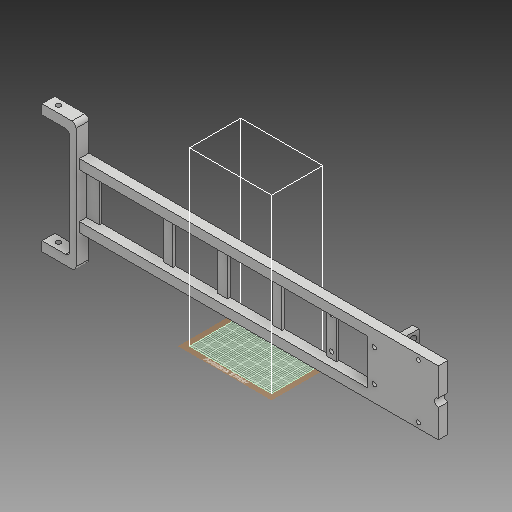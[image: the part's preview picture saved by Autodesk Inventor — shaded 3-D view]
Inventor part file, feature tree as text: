
AUTODESK INVENTOR PART (.ipt)
format: ipt  version: 2019 (Build 230136000, 136)  size: 610,816 bytes
history: native  units: mm
features: sketch x34, extrude x25, fillet x6, hole x5
ambient origin geometry x8: Origin, YZ Plane, XZ Plane, XY Plane, X Axis, Y Axis, Z Axis, Center Point
bodies: Solid1 (feature_tree)
feature tree (70):
  extrude  "Extrusion1"  Depth=50.0mm
  hole  "Hole1"  [1 undecoded]
  hole  "Hole2"  [1 undecoded]
  extrude  "Extrusion2"  Depth=25.0mm
  extrude  "Extrusion3"  Depth=25.0mm
  extrude  "Extrusion4"  Depth=5.0mm
  sketch  "Sketch7"  dims[d25=10.0mm d26=5.0mm]
  extrude  "Extrusion5"  Depth=5.0mm
  extrude  "Extrusion6"  Depth=35.0mm
  extrude  "Extrusion7"  Depth=35.0mm
  extrude  "Extrusion8"  Depth=35.0mm
  extrude  "Extrusion9"  Depth=2.0mm TaperAngle=0.0deg
  extrude  "Extrusion10"  Depth=7.5mm TaperAngle=0.0deg
  extrude  "Extrusion11"  Depth=10.0mm
  extrude  "Extrusion12"  Depth=7.5mm
  fillet  "Fillet1"  Radius=7.5mm
  fillet  "Fillet2"  Radius=25.0mm
  fillet  "Fillet3"  Radius=3.0mm
  fillet  "Fillet4"  Radius=3.2mm
  fillet  "Fillet5"  Radius=2.1mm
  fillet  "Fillet6"  Radius=5.5mm
  extrude  "Extrusion13"  Depth=92.5mm TaperAngle=0.0deg
  sketch  "Sketch17"  dims[d58=4.25mm d59=241.0mm d60=0.0mm]
  hole  "Hole3"  [1 undecoded]
  hole  "Hole4"  [1 undecoded]
  extrude  "Extrusion14"  Depth=5.0mm
  extrude  "Extrusion15"  Depth=91.25mm TaperAngle=0.0deg
  extrude  "Extrusion16"  Depth=30.0mm
  extrude  "Extrusion17"  Depth=2.5mm
  extrude  "Extrusion18"  Depth=14.55mm TaperAngle=0.0deg
  extrude  "Extrusion19"  Depth=0.1mm
  extrude  "Extrusion20"  Depth=3.25mm
  extrude  "Extrusion21"  Depth=3.25mm
  hole  "Hole5"  [1 undecoded]
  extrude  "Extrusion22"  Depth=2.0mm
  extrude  "Extrusion23"  Depth=15.0mm
  sketch  "Sketch31"  dims[d102=20.0mm d103=0.0mm d104=10.0mm d105=0.0mm]
  sketch  "Sketch32"  dims[d106=2.0mm d107=0.0mm d108=4.0mm]
  extrude  "Extrusion24"  Depth=10.0mm TaperAngle=0.0deg
  extrude  "Extrusion25"  Depth=4.0mm
  sketch  "Sketch1"  dims[d0=50.0mm d1=50.0mm]
  sketch  "Sketch2"  dims[d2=240.0mm d3=7.5mm]
  sketch  "Sketch3"  dims[d4=7.5mm d5=7.5mm d6=0.0mm]
  sketch  "Sketch4"  dims[d7=6.35mm d8=6.0mm d9=4.0mm d10=2.0mm d11=90.0deg d12=8.0mm d13=20.594885mm d14=25.0mm]
  sketch  "Sketch5"  dims[d15=3.3mm d16=6.0mm d17=4.0mm d18=2.0mm d19=90.0deg d20=8.0mm d21=20.594885mm d22=25.0mm]
  sketch  "Sketch6"  dims[d23=180.0deg d24=5.0mm]
  sketch  "Sketch8"  dims[d27=17.5mm d28=0.0mm d30=35.0mm]
  sketch  "Sketch9"  dims[d31=35.0mm d32=35.0mm]
  sketch  "Sketch10"  dims[d33=35.0mm d34=35.0mm]
  sketch  "Sketch11"  dims[d35=35.0mm d36=2.0mm d37=0.0mm]
  sketch  "Sketch12"  dims[d38=10.0mm d39=7.5mm d40=0.0mm]
  sketch  "Sketch13"  dims[d41=100.0mm d42=10.0mm]
  sketch  "Sketch14"  dims[d43=7.5mm d44=0.0mm d45=7.5mm d46=7.5mm d47=25.0mm d48=0.0mm d49=3.0mm d50=3.2mm d51=2.1mm d52=5.5mm]
  sketch  "Sketch15"  dims[d53=3.3mm d54=92.5mm d55=0.0mm]
  sketch  "Sketch16"  dims[d56=5.5mm d57=3.3mm]
  sketch  "Sketch18"  dims[d61=4.44mm d62=5.0mm]
  sketch  "Sketch19"  dims[d63=2.5mm d64=91.25mm d65=0.0mm]
  sketch  "Sketch20"  dims[d66=30.0mm d67=6.35mm]
  sketch  "Sketch21"  dims[d68=3.8mm d69=0.0mm d70=2.5mm]
  sketch  "Sketch22"  dims[d71=14.55mm d72=0.0mm d73=14.55mm d74=0.0mm]
  sketch  "Sketch23"  dims[d75=0.1mm d76=0.1mm]
  sketch  "Sketch24"  dims[d77=3.25mm d78=3.25mm]
  sketch  "Sketch25"  dims[d79=3.25mm d80=3.25mm]
  sketch  "Sketch26"  dims[d81=35.0mm d82=10.0mm]
  sketch  "Sketch27"  dims[d83=2.0mm d84=0.0mm d85=3.6mm]
  sketch  "Sketch28"  dims[d86=3.6mm]
  sketch  "Sketch29"  dims[d87=3.3mm d88=6.0mm d89=4.0mm d90=2.0mm d91=90.0deg d92=15.0mm d93=20.594885mm]
  sketch  "Sketch30"  dims[d94=3.3mm d95=6.0mm d96=4.0mm d97=2.0mm d98=90.0deg d99=15.0mm d100=20.594885mm d101=6.0mm]
  sketch  "Sketch33"  dims[d109=100.0mm d110=0.0mm]
  sketch  "Sketch34"  dims[d111=100.0mm d112=0.0mm d113=5.0mm d114=2.0mm d115=0.0mm d116=3.3mm d117=3.3mm d118=3.3mm d119=3.3mm d120=2.0mm d121=0.0mm d122=5.5mm d123=0.0mm d124=3.3mm d125=6.0mm d126=4.0mm d127=2.0mm d128=90.0deg d129=8.0mm d130=20.594885mm d131=42.0mm d132=17.0mm d133=21.0mm d135=8.5mm d136=15.825mm d137=3.5mm d138=21.0mm d139=3.3mm d140=3.3mm d141=3.3mm d142=10.0mm d143=0.0mm d144=7.5mm d145=0.0mm d146=100.0mm d147=0.0mm d148=4.0mm d149=4.0mm d150=4.0mm d151=4.0mm d152=10.0mm d153=0.0mm]
note: 5 required parameter values undecoded (feature->parameter linkage not recoverable at this tier; creation-order binding heuristic only, values carry confidence <= 0.55)
